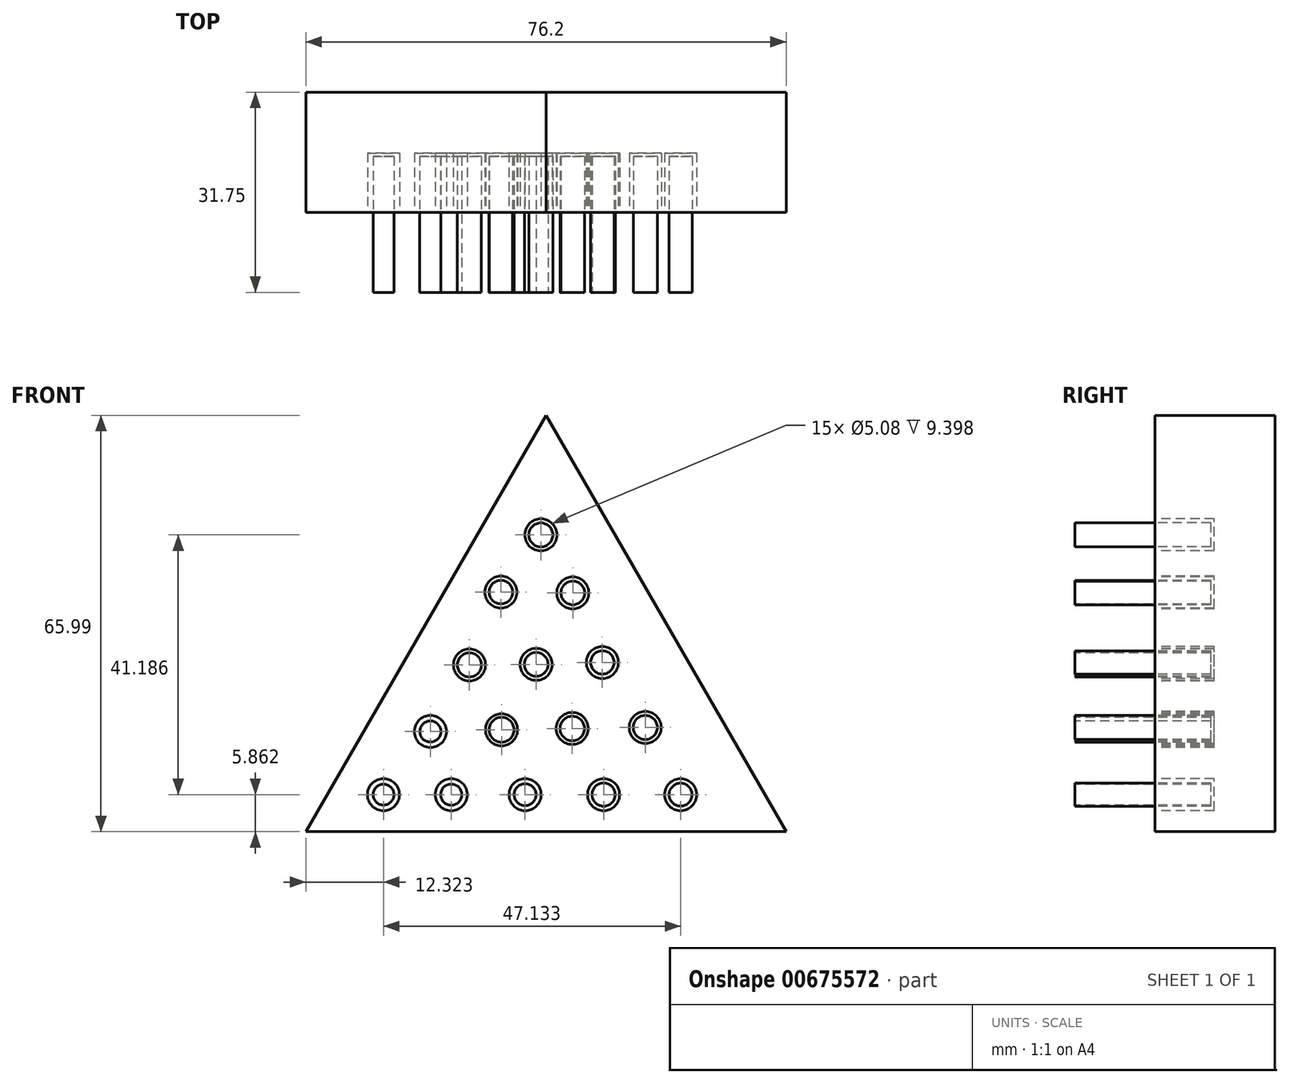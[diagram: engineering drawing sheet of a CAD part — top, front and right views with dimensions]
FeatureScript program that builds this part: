
annotation { "Feature Type Name" : "Feature", "Feature Type Description" : "" }
export const myFeature = defineFeature(function(context is Context, id is Id, definition is map)
    precondition{}
    {
        {
            var Q0;
            Q0=qCreatedBy(makeId("Front.planeOp"),FACE);
            var sketch = newSketch(context, id + "F0", { "sketchPlane" : qUnion([Q0])});
            skLineSegment(sketch, "E0", {"start": v(-76.2, 0) * mm, "end": v(-38.1, 66) * mm});
            skLineSegment(sketch, "E1", {"start": v(-38.1, 66) * mm, "end": v(0, 0) * mm});
            skLineSegment(sketch, "E2", {"start": v(0, 0) * mm, "end": v(-76.2, 0) * mm});
            skSolve(sketch);
        }
        {
            var Q0;
            Q0=makeQuery(id+"F0.imprint","IMPRINT",FACE,{"disambiguationData":[TD([[makeQuery(id+"F0.imprint","IMPRINT",EDGE,{"derivedFrom":sQuery(id+"F0.wireOp",EDGE,"E0")}),-1.0]])]});
            extrude(context, id + "F1", {"entities" : qUnion([Q0]), "depth" : 19.05 * mm, "offsetDistance" : 25.4 * mm});
        }
        {
            var Q0;
            Q0=makeQuery(id+"F1.opExtrude","CAP_FACE",FACE,{"disambiguationData":[OSD([sQuery(id+"F0.wireOp",EDGE,"E0"),sQuery(id+"F0.wireOp",EDGE,"E1"),sQuery(id+"F0.wireOp",EDGE,"E2")])],"isStart":false});
            var sketch = newSketch(context, id + "F2", { "sketchPlane" : qUnion([Q0])});
            skCircle(sketch, "E3", {"center": v(-63.88, 5.86) * mm, "radius": 2.54 * mm});
            skCircle(sketch, "E4", {"center": v(-53.13, 5.86) * mm, "radius": 2.54 * mm});
            skCircle(sketch, "E5", {"center": v(-41.41, 5.86) * mm, "radius": 2.54 * mm});
            skCircle(sketch, "E6", {"center": v(-28.96, 5.86) * mm, "radius": 2.54 * mm});
            skCircle(sketch, "E7", {"center": v(-16.74, 5.86) * mm, "radius": 2.54 * mm});
            skSolve(sketch);
        }
        {
            var Q0;
            Q0 = qSketchRegion(id + "F2", true);
            extrude(context, id + "F3", {"entities" : qUnion([Q0]), "operationType" : NewBodyOperationType.REMOVE, "oppositeDirection" : true, "depth" : 9.4 * mm, "offsetDistance" : 25.4 * mm});
        }
        {
            var Q0;
            Q0=makeQuery(id+"F1.opExtrude","CAP_FACE",FACE,{"disambiguationData":[OSD([sQuery(id+"F0.wireOp",EDGE,"E0"),sQuery(id+"F0.wireOp",EDGE,"E1"),sQuery(id+"F0.wireOp",EDGE,"E2")])],"isStart":false});
            var sketch = newSketch(context, id + "F4", { "sketchPlane" : qUnion([Q0])});
            skCircle(sketch, "E8", {"center": v(-22.35, 16.51) * mm, "radius": 2.54 * mm});
            skCircle(sketch, "E9", {"center": v(-33.93, 16.35) * mm, "radius": 2.54 * mm});
            skCircle(sketch, "E10", {"center": v(-45.15, 16.15) * mm, "radius": 2.54 * mm});
            skCircle(sketch, "E11", {"center": v(-56.44, 15.87) * mm, "radius": 2.54 * mm});
            skSolve(sketch);
        }
        {
            var Q0;
            Q0 = qSketchRegion(id + "F4", true);
            extrude(context, id + "F5", {"entities" : qUnion([Q0]), "operationType" : NewBodyOperationType.REMOVE, "oppositeDirection" : true, "depth" : 9.4 * mm, "offsetDistance" : 25.4 * mm});
        }
        {
            var Q0;
            Q0=makeQuery(id+"F1.opExtrude","CAP_FACE",FACE,{"disambiguationData":[OSD([sQuery(id+"F0.wireOp",EDGE,"E0"),sQuery(id+"F0.wireOp",EDGE,"E1"),sQuery(id+"F0.wireOp",EDGE,"E2")])],"isStart":false});
            var sketch = newSketch(context, id + "F6", { "sketchPlane" : qUnion([Q0])});
            skCircle(sketch, "E12", {"center": v(-50.24, 26.43) * mm, "radius": 2.54 * mm});
            skCircle(sketch, "E13", {"center": v(-39.64, 26.52) * mm, "radius": 2.54 * mm});
            skCircle(sketch, "E14", {"center": v(-29.16, 26.82) * mm, "radius": 2.54 * mm});
            skSolve(sketch);
        }
        {
            var Q0;
            Q0 = qSketchRegion(id + "F6", true);
            extrude(context, id + "F7", {"entities" : qUnion([Q0]), "operationType" : NewBodyOperationType.REMOVE, "oppositeDirection" : true, "depth" : 9.4 * mm, "offsetDistance" : 25.4 * mm});
        }
        {
            var Q0;
            Q0=makeQuery(id+"F1.opExtrude","CAP_FACE",FACE,{"disambiguationData":[OSD([sQuery(id+"F0.wireOp",EDGE,"E0"),sQuery(id+"F0.wireOp",EDGE,"E1"),sQuery(id+"F0.wireOp",EDGE,"E2")])],"isStart":false});
            var sketch = newSketch(context, id + "F8", { "sketchPlane" : qUnion([Q0])});
            skCircle(sketch, "E15", {"center": v(-45.25, 37.97) * mm, "radius": 2.54 * mm});
            skCircle(sketch, "E16", {"center": v(-33.85, 37.84) * mm, "radius": 2.54 * mm});
            skSolve(sketch);
        }
        {
            var Q0;
            Q0 = qSketchRegion(id + "F8", true);
            extrude(context, id + "F9", {"entities" : qUnion([Q0]), "operationType" : NewBodyOperationType.REMOVE, "oppositeDirection" : true, "depth" : 9.4 * mm, "offsetDistance" : 25.4 * mm});
        }
        {
            var Q0;
            Q0=makeQuery(id+"F1.opExtrude","CAP_FACE",FACE,{"disambiguationData":[OSD([sQuery(id+"F0.wireOp",EDGE,"E0"),sQuery(id+"F0.wireOp",EDGE,"E1"),sQuery(id+"F0.wireOp",EDGE,"E2")])],"isStart":false});
            var sketch = newSketch(context, id + "F10", { "sketchPlane" : qUnion([Q0])});
            skCircle(sketch, "E17", {"center": v(-38.92, 47.05) * mm, "radius": 2.54 * mm});
            skSolve(sketch);
        }
        {
            var Q0;
            Q0 = qSketchRegion(id + "F10", true);
            extrude(context, id + "F11", {"entities" : qUnion([Q0]), "operationType" : NewBodyOperationType.REMOVE, "oppositeDirection" : true, "depth" : 9.4 * mm, "offsetDistance" : 25.4 * mm});
        }
        {
            var Q0;
            Q0=makeQuery(id+"F1.opExtrude","CAP_FACE",FACE,{"disambiguationData":[OSD([sQuery(id+"F0.wireOp",EDGE,"E0"),sQuery(id+"F0.wireOp",EDGE,"E1"),sQuery(id+"F0.wireOp",EDGE,"E2")])],"isStart":false});
            var sketch = newSketch(context, id + "F12", { "sketchPlane" : qUnion([Q0])});
            skCircle(sketch, "E18", {"center": v(-38.92, 47.05) * mm, "radius": 1.9 * mm});
            skSolve(sketch);
        }
        {
            var Q0;
            Q0 = qSketchRegion(id + "F12", true);
            extrude(context, id + "F13", {"entities" : qUnion([Q0]), "oppositeDirection" : true, "depth" : 8.9 * mm, "offsetDistance" : 25.4 * mm, "hasSecondDirection" : true, "secondDirectionOppositeDirection" : false, "secondDirectionDepth" : 12.7 * mm});
        }
        {
            var Q0;
            Q0=makeQuery(id+"F1.opExtrude","CAP_FACE",FACE,{"disambiguationData":[OSD([sQuery(id+"F0.wireOp",EDGE,"E0"),sQuery(id+"F0.wireOp",EDGE,"E1"),sQuery(id+"F0.wireOp",EDGE,"E2")])],"isStart":false});
            var sketch = newSketch(context, id + "F14", { "sketchPlane" : qUnion([Q0])});
            skCircle(sketch, "E19", {"center": v(-16.74, 5.86) * mm, "radius": 1.82 * mm});
            skCircle(sketch, "E20", {"center": v(-28.96, 5.86) * mm, "radius": 1.84 * mm});
            skCircle(sketch, "E21", {"center": v(-41.41, 5.86) * mm, "radius": 1.74 * mm});
            skCircle(sketch, "E22", {"center": v(-53.13, 5.86) * mm, "radius": 1.68 * mm});
            skCircle(sketch, "E23", {"center": v(-63.88, 5.86) * mm, "radius": 1.66 * mm});
            skCircle(sketch, "E24", {"center": v(-45.25, 37.97) * mm, "radius": 1.87 * mm});
            skCircle(sketch, "E25", {"center": v(-33.85, 37.84) * mm, "radius": 1.88 * mm});
            skCircle(sketch, "E26", {"center": v(-50.24, 26.43) * mm, "radius": 1.9 * mm});
            skCircle(sketch, "E27", {"center": v(-39.64, 26.52) * mm, "radius": 1.88 * mm});
            skCircle(sketch, "E28", {"center": v(-56.44, 15.87) * mm, "radius": 1.67 * mm});
            skCircle(sketch, "E29", {"center": v(-45.15, 16.15) * mm, "radius": 1.98 * mm});
            skCircle(sketch, "E30", {"center": v(-33.93, 16.35) * mm, "radius": 1.95 * mm});
            skCircle(sketch, "E31", {"center": v(-22.35, 16.51) * mm, "radius": 1.9 * mm});
            skCircle(sketch, "E32", {"center": v(-29.16, 26.82) * mm, "radius": 1.85 * mm});
            skSolve(sketch);
        }
        {
            var Q0;
            Q0 = qSketchRegion(id + "F14", true);
            extrude(context, id + "F15", {"entities" : qUnion([Q0]), "oppositeDirection" : true, "depth" : 8.9 * mm, "offsetDistance" : 25.4 * mm, "hasSecondDirection" : true, "secondDirectionOppositeDirection" : false, "secondDirectionDepth" : 12.7 * mm});
        }
    });
